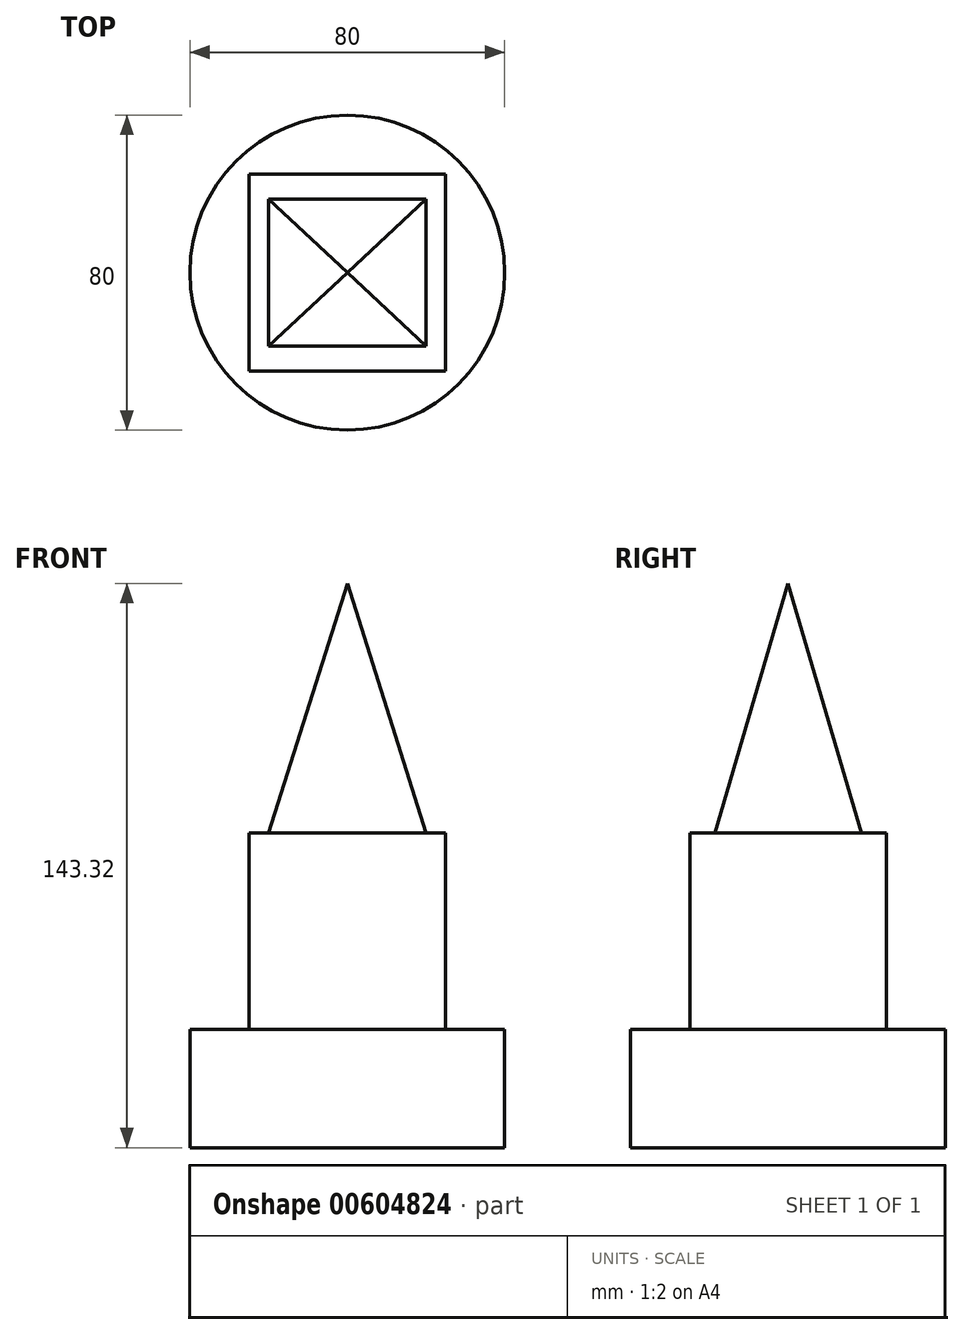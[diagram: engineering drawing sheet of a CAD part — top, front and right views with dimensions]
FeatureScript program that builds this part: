
annotation { "Feature Type Name" : "Feature", "Feature Type Description" : "" }
export const myFeature = defineFeature(function(context is Context, id is Id, definition is map)
    precondition{}
    {
        {
            var Q0;
            Q0=qCreatedBy(makeId("Top.planeOp"),FACE);
            var sketch = newSketch(context, id + "F0", { "sketchPlane" : qUnion([Q0])});
            skCircle(sketch, "E0", {"center": v(0, 0) * mm, "radius": 40 * mm});
            skSolve(sketch);
        }
        {
            var Q0;
            Q0 = qSketchRegion(id + "F0", true);
            extrude(context, id + "F1", {"entities" : qUnion([Q0]), "depth" : 30 * mm, "offsetDistance" : 25.4 * mm});
        }
        {
            var Q0;
            Q0=makeQuery(id+"F1.opExtrude","CAP_FACE",FACE,{"disambiguationData":[OSD([sQuery(id+"F0.wireOp",EDGE,"E0")])],"isStart":false});
            var sketch = newSketch(context, id + "F2", { "sketchPlane" : qUnion([Q0])});
            skLineSegment(sketch, "E1.bottom", {"start": v(25, -25) * mm, "end": v(-25, -25) * mm});
            skLineSegment(sketch, "E1.top", {"start": v(25, 25) * mm, "end": v(-25, 25) * mm});
            skLineSegment(sketch, "E1.left", {"start": v(25, -25) * mm, "end": v(25, 25) * mm});
            skLineSegment(sketch, "E1.right", {"start": v(-25, -25) * mm, "end": v(-25, 25) * mm});
            skPoint(sketch, "E1.middle", {"position": v(0, 0) * mm});
            skSolve(sketch);
        }
        {
            var Q0;
            Q0 = qSketchRegion(id + "F2", true);
            extrude(context, id + "F3", {"entities" : qUnion([Q0]), "operationType" : NewBodyOperationType.ADD, "depth" : 50 * mm, "offsetDistance" : 25.4 * mm});
        }
        {
            var Q0;
            Q0=makeQuery(id+"F3.opExtrude","CAP_FACE",FACE,{"disambiguationData":[OSD([sQuery(id+"F2.wireOp",EDGE,"E1.bottom"),sQuery(id+"F2.wireOp",EDGE,"E1.top"),sQuery(id+"F2.wireOp",EDGE,"E1.left"),sQuery(id+"F2.wireOp",EDGE,"E1.right")])],"isStart":false});
            var sketch = newSketch(context, id + "F4", { "sketchPlane" : qUnion([Q0])});
            skLineSegment(sketch, "E2.bottom", {"start": v(20, 18.65) * mm, "end": v(-20, 18.65) * mm});
            skLineSegment(sketch, "E2.top", {"start": v(20, -18.65) * mm, "end": v(-20, -18.65) * mm});
            skLineSegment(sketch, "E2.left", {"start": v(20, 18.65) * mm, "end": v(20, -18.65) * mm});
            skLineSegment(sketch, "E2.right", {"start": v(-20, 18.65) * mm, "end": v(-20, -18.65) * mm});
            skPoint(sketch, "E2.middle", {"position": v(0, 0) * mm});
            skSolve(sketch);
        }
        {
            var Q0;
            Q0=qCreatedBy(makeId("Right.planeOp"),FACE);
            var sketch = newSketch(context, id + "F5", { "sketchPlane" : qUnion([Q0])});
            skLineSegment(sketch, "E3", {"start": v(0, 73.32) * mm, "end": v(0, 143.32) * mm});
            skSolve(sketch);
        }
        {
            var Q1;
            Q1=sQuery(id+"F5.wireOp",VERTEX,"E3.end");
            var Q2;
            Q2=makeQuery(id+"F4.imprint","IMPRINT",FACE,{"disambiguationData":[TD([[makeQuery(id+"F4.imprint","IMPRINT",EDGE,{"derivedFrom":sQuery(id+"F4.wireOp",EDGE,"E2.bottom")}),1.0]])]});
            loft(context, id + "F6", {"operationType" : NewBodyOperationType.ADD, "sheetProfilesArray" : [{ "sheetProfileEntities" : qUnion([Q1]) }, { "sheetProfileEntities" : qUnion([Q2]) }]});
        }
    });
